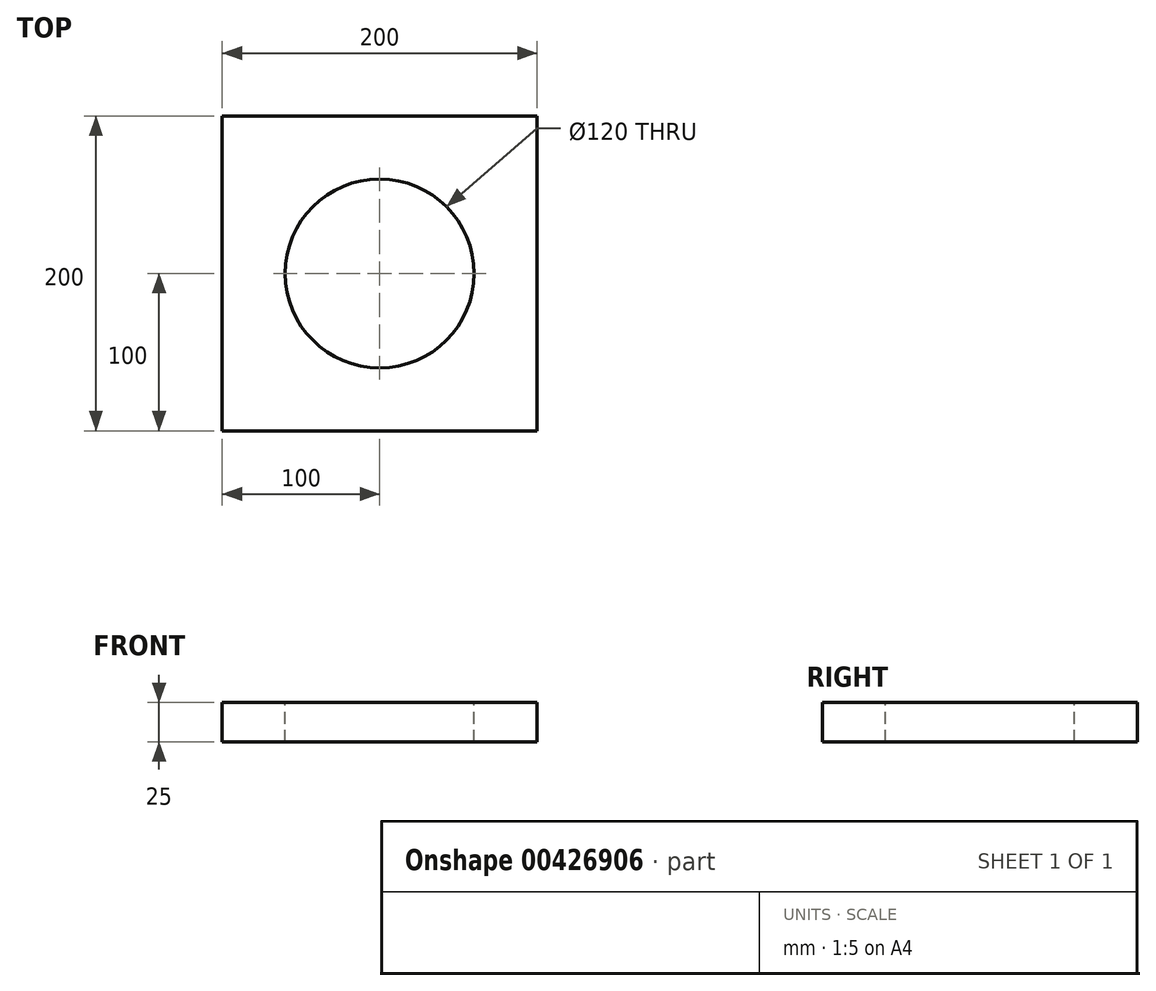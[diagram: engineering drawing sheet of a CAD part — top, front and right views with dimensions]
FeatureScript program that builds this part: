
annotation { "Feature Type Name" : "Feature", "Feature Type Description" : "" }
export const myFeature = defineFeature(function(context is Context, id is Id, definition is map)
    precondition{}
    {
        {
            var Q0;
            Q0=qCreatedBy(makeId("Top.planeOp"),FACE);
            var sketch = newSketch(context, id + "F0", { "sketchPlane" : qUnion([Q0])});
            skLineSegment(sketch, "E0.bottom", {"start": v(100, 100) * mm, "end": v(-100, 100) * mm});
            skLineSegment(sketch, "E0.top", {"start": v(100, -100) * mm, "end": v(-100, -100) * mm});
            skLineSegment(sketch, "E0.left", {"start": v(100, 100) * mm, "end": v(100, -100) * mm});
            skLineSegment(sketch, "E0.right", {"start": v(-100, 100) * mm, "end": v(-100, -100) * mm});
            skPoint(sketch, "E0.middle", {"position": v(0, 0) * mm});
            skSolve(sketch);
        }
        {
            var Q0;
            Q0 = qSketchRegion(id + "F0", true);
            extrude(context, id + "F1", {"entities" : qUnion([Q0]), "depth" : 25 * mm});
        }
        {
            var Q0;
            Q0=makeQuery(id+"F1.opExtrude","CAP_FACE",FACE,{"disambiguationData":[OSD([sQuery(id+"F0.wireOp",EDGE,"E0.bottom"),sQuery(id+"F0.wireOp",EDGE,"E0.top"),sQuery(id+"F0.wireOp",EDGE,"E0.left"),sQuery(id+"F0.wireOp",EDGE,"E0.right")])],"isStart":false});
            var sketch = newSketch(context, id + "F2", { "sketchPlane" : qUnion([Q0])});
            skCircle(sketch, "E1", {"center": v(0, 0) * mm, "radius": 60 * mm});
            skSolve(sketch);
        }
        {
            var Q0;
            Q0=makeQuery(id+"F2.imprint","IMPRINT",FACE,{"disambiguationData":[TD([[makeQuery(id+"F2.imprint","IMPRINT",EDGE,{"derivedFrom":sQuery(id+"F2.wireOp",EDGE,"E1")}),1.0]])]});
            var Q1;
            Q1=makeQuery(id+"F1.opExtrude","CAP_FACE",FACE,{"disambiguationData":[OSD([sQuery(id+"F0.wireOp",EDGE,"E0.bottom"),sQuery(id+"F0.wireOp",EDGE,"E0.top"),sQuery(id+"F0.wireOp",EDGE,"E0.left"),sQuery(id+"F0.wireOp",EDGE,"E0.right")])],"isStart":true});
            extrude(context, id + "F3", {"entities" : qUnion([Q0]), "operationType" : NewBodyOperationType.REMOVE, "endBound" : BoundingType.UP_TO_SURFACE, "oppositeDirection" : true, "endBoundEntityFace" : qUnion([Q1]), "depth" : 25 * mm});
        }
    });
